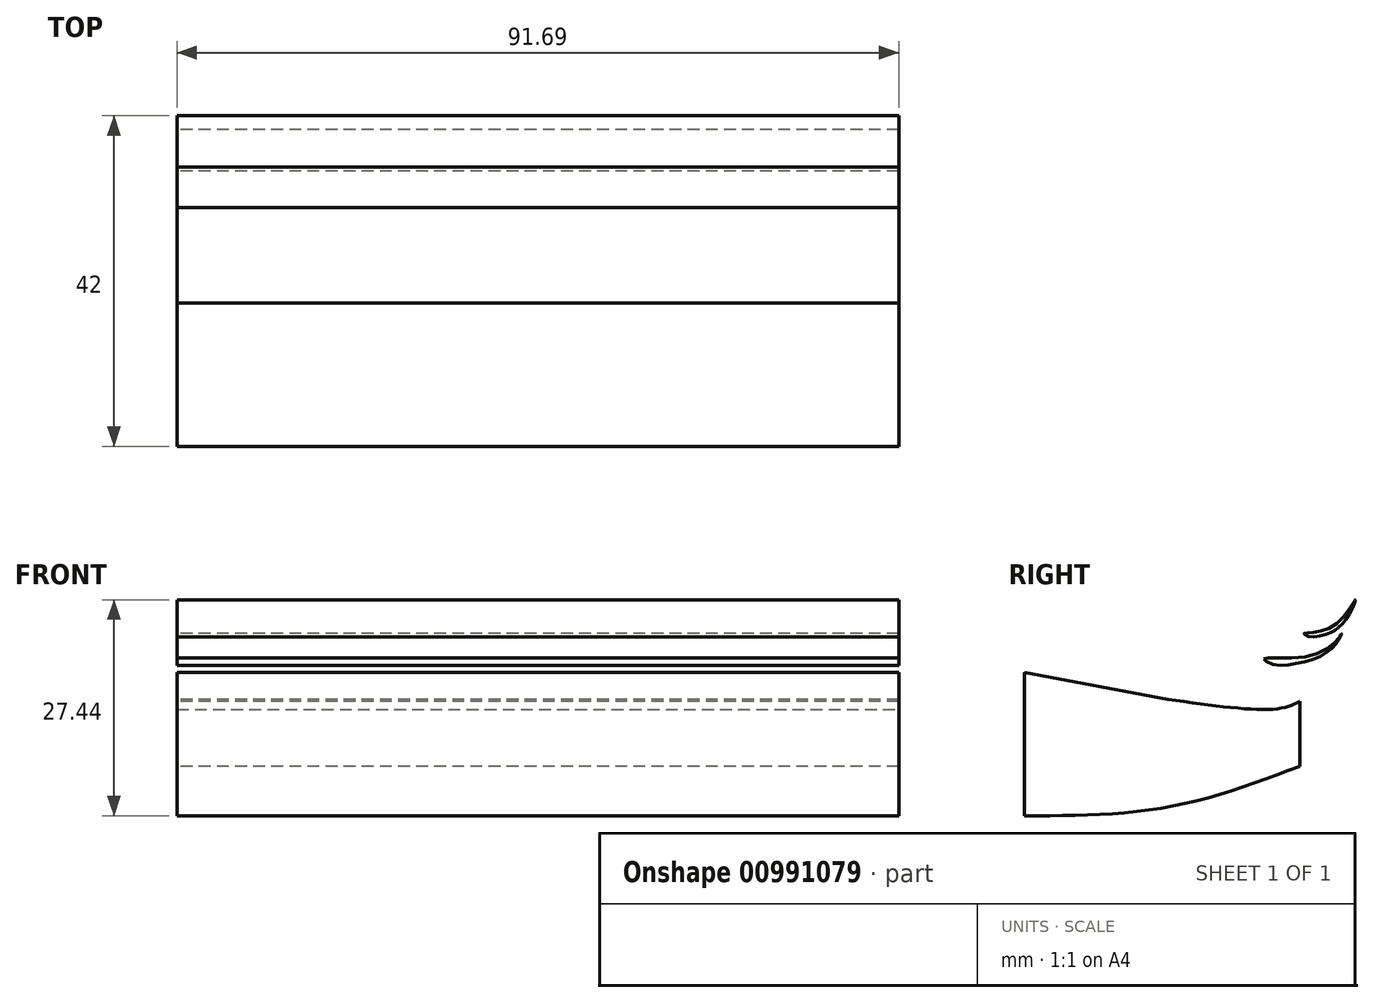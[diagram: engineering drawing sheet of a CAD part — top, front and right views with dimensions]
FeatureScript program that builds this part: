
annotation { "Feature Type Name" : "Feature", "Feature Type Description" : "" }
export const myFeature = defineFeature(function(context is Context, id is Id, definition is map)
    precondition{}
    {
        {
            var Q0;
            Q0=qCreatedBy(makeId("Right.planeOp"),FACE);
            var sketch = newSketch(context, id + "F0", { "sketchPlane" : qUnion([Q0])});
            skFitSpline(sketch, "E0", {"points": [v(-21.67, 13.67) * mm, v(-8.03, 12.44) * mm, v(-4.9, 13.38) * mm], "startDerivative": vector(23.93, -3.41) * mm, "endDerivative": vector(7.76, 3.64) * mm});
            skLineSegment(sketch, "E1", {"start": v(-4.9, 13.38) * mm, "end": v(-4.9, 5.16) * mm});
            skFitSpline(sketch, "E2", {"points": [v(-4.9, 5.16) * mm, v(-21.56, 0) * mm, v(-39.85, -1.13) * mm], "startDerivative": vector(-33.14, -12.47) * mm, "endDerivative": vector(-36.74, -0.15) * mm});
            skLineSegment(sketch, "E3", {"start": v(-39.85, -1.13) * mm, "end": v(-39.85, 17.11) * mm});
            skFitSpline(sketch, "E4", {"points": [v(-39.85, 17.11) * mm, v(-21.67, 13.67) * mm], "startDerivative": vector(18.18, -3.44) * mm, "endDerivative": vector(18.18, -3.44) * mm});
            skFitSpline(sketch, "E5", {"points": [v(-9.49, 18.8) * mm, v(-4.36, 19.05) * mm, v(0, 21.37) * mm, v(0.4, 22.02) * mm, v(0.28, 21.65) * mm, v(-0.5, 20.5) * mm, v(-2.22, 19.18) * mm, v(-5.44, 18.2) * mm, v(-8.26, 18.12) * mm, v(-9.49, 18.8) * mm]});
            skFitSpline(sketch, "E6", {"points": [v(-3.92, 22.09) * mm, v(0, 23.45) * mm, v(2.14, 26.31) * mm, v(1.46, 24.62) * mm, v(0, 22.76) * mm, v(-1.31, 22.02) * mm, v(-3.64, 21.64) * mm, v(-4.36, 22.02) * mm, v(-3.92, 22.09) * mm]});
            skSolve(sketch);
        }
        {
            var Q0;
            Q0 = qSketchRegion(id + "F0", true);
            extrude(context, id + "F1", {"entities" : qUnion([Q0]), "depth" : 91.7 * mm, "offsetDistance" : 25.4 * mm});
        }
    });
